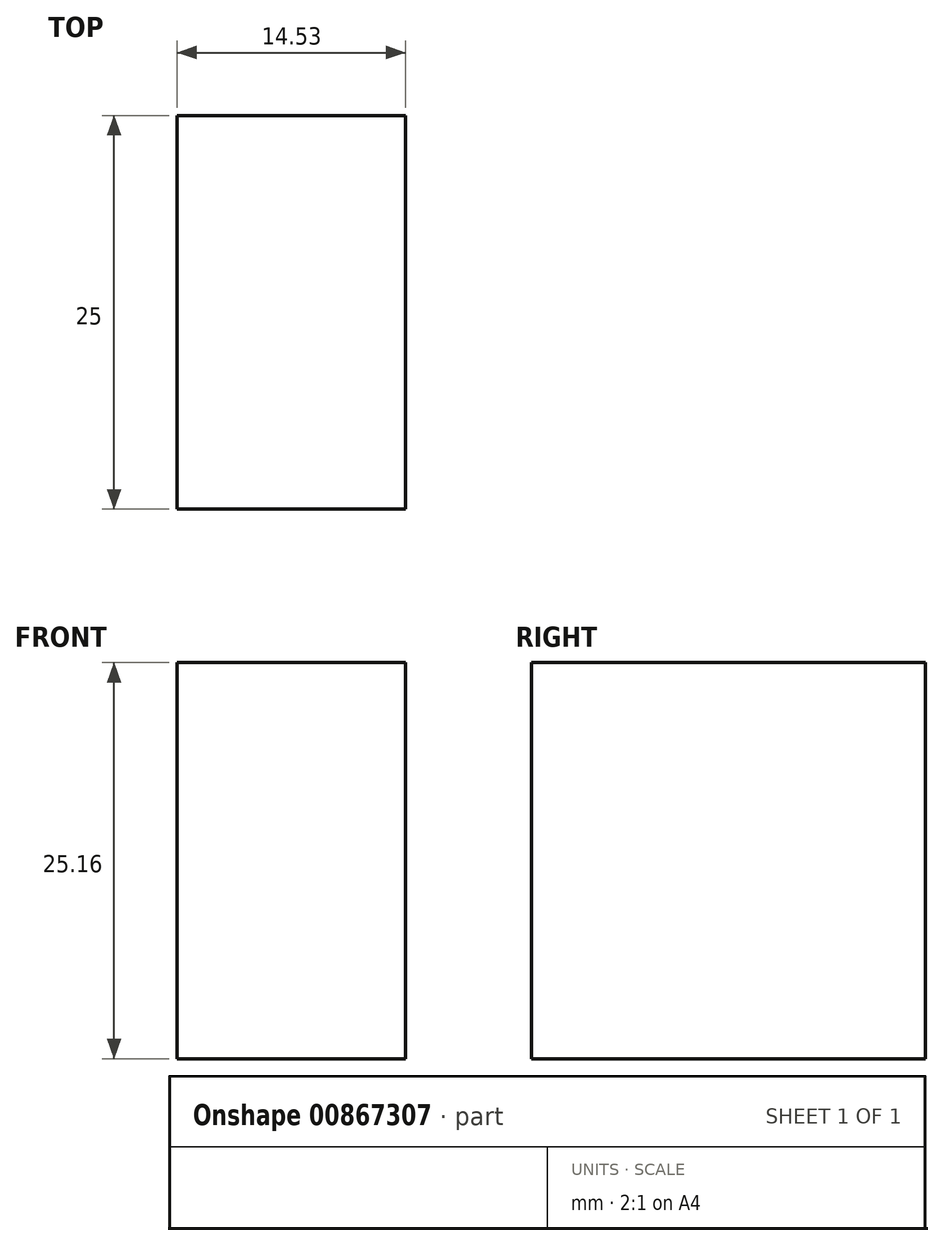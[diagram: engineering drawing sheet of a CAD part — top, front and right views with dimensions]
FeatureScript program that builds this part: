
annotation { "Feature Type Name" : "Feature", "Feature Type Description" : "" }
export const myFeature = defineFeature(function(context is Context, id is Id, definition is map)
    precondition{}
    {
        {
            var Q0;
            Q0=qCreatedBy(makeId("Front.planeOp"),FACE);
            var sketch = newSketch(context, id + "F0", { "sketchPlane" : qUnion([Q0])});
            skLineSegment(sketch, "E0.bottom", {"start": v(-79.22, 41.48) * mm, "end": v(79.22, 41.48) * mm});
            skLineSegment(sketch, "E0.top", {"start": v(-79.22, -41.48) * mm, "end": v(79.22, -41.48) * mm});
            skLineSegment(sketch, "E0.left", {"start": v(-79.22, 41.48) * mm, "end": v(-79.22, -41.48) * mm});
            skLineSegment(sketch, "E0.right", {"start": v(79.22, 41.48) * mm, "end": v(79.22, -41.48) * mm});
            skPoint(sketch, "E0.middle", {"position": v(0, 0) * mm});
            skLineSegment(sketch, "E1.bottom", {"start": v(-53.33, 0) * mm, "end": v(-67.86, 0) * mm});
            skLineSegment(sketch, "E1.top", {"start": v(-53.33, 25.16) * mm, "end": v(-67.86, 25.16) * mm});
            skLineSegment(sketch, "E1.left", {"start": v(-53.33, 0) * mm, "end": v(-53.33, 25.16) * mm});
            skLineSegment(sketch, "E1.right", {"start": v(-67.86, 0) * mm, "end": v(-67.86, 25.16) * mm});
            skPoint(sketch, "E1.middle", {"position": v(-60.6, 12.58) * mm});
            skSolve(sketch);
        }
        {
            var Q0;
            Q0=makeQuery(id+"F0.imprint","IMPRINT",FACE,{"disambiguationData":[TD([[makeQuery(id+"F0.imprint","IMPRINT",EDGE,{"derivedFrom":sQuery(id+"F0.wireOp",EDGE,"E1.bottom")}),-1.0]])]});
            extrude(context, id + "F1", {"entities" : qUnion([Q0]), "depth" : 25 * mm, "offsetDistance" : 25 * mm});
        }
    });
